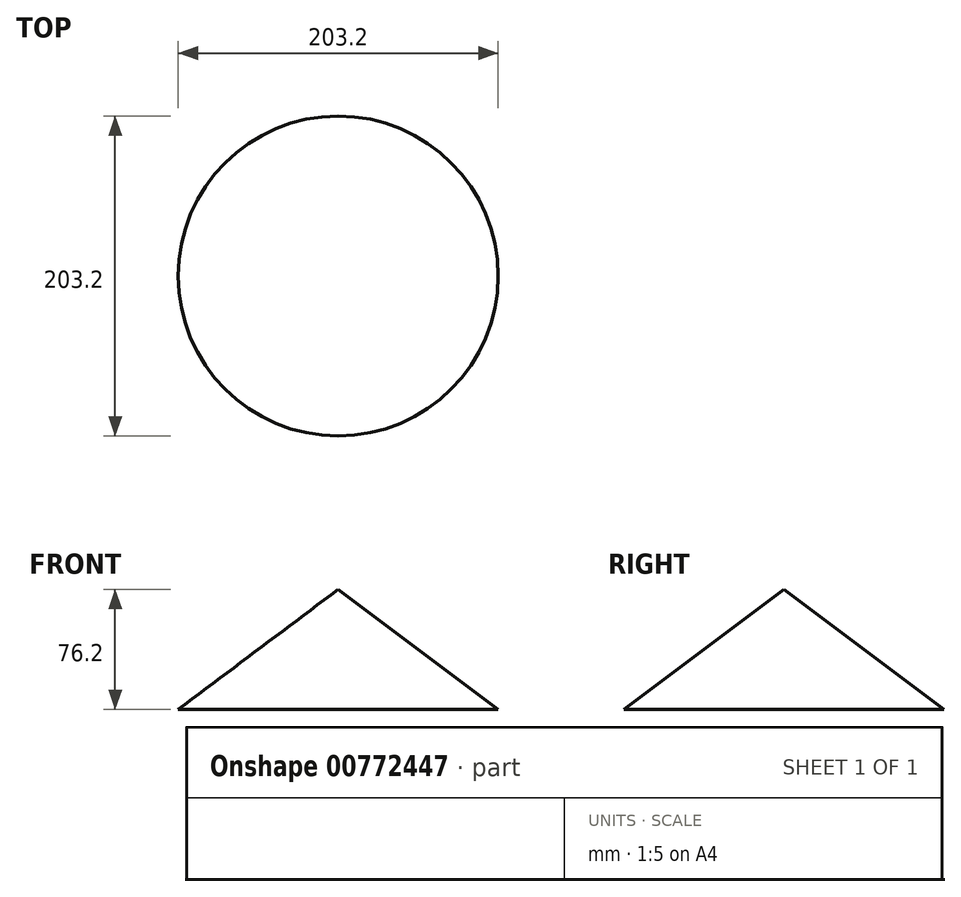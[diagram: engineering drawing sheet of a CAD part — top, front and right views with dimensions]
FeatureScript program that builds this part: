
annotation { "Feature Type Name" : "Feature", "Feature Type Description" : "" }
export const myFeature = defineFeature(function(context is Context, id is Id, definition is map)
    precondition{}
    {
        {
            var Q0;
            Q0=qCreatedBy(makeId("Front.planeOp"),FACE);
            var sketch = newSketch(context, id + "F0", { "sketchPlane" : qUnion([Q0])});
            skLineSegment(sketch, "E0", {"start": v(0, 0) * mm, "end": v(0, 76.2) * mm});
            skLineSegment(sketch, "E1", {"start": v(0, 76.2) * mm, "end": v(101.6, 0) * mm});
            skLineSegment(sketch, "E2", {"start": v(101.6, 0) * mm, "end": v(0, 0) * mm});
            skSolve(sketch);
        }
        {
            var Q0;
            Q0=makeQuery(id+"F0.imprint","IMPRINT",FACE,{"disambiguationData":[TD([[makeQuery(id+"F0.imprint","IMPRINT",EDGE,{"derivedFrom":sQuery(id+"F0.wireOp",EDGE,"E0")}),-1.0]])]});
            var Q1;
            Q1=sQuery(id+"F0.wireOp",EDGE,"E0");
            revolve(context, id + "F1", {"surfaceOperationType" : NewSurfaceOperationType.NEW, "entities" : qUnion([Q0]), "axis" : qUnion([Q1]), "revolveType" : RevolveType.ONE_DIRECTION, "angle" : 360 * degree});
        }
    });
